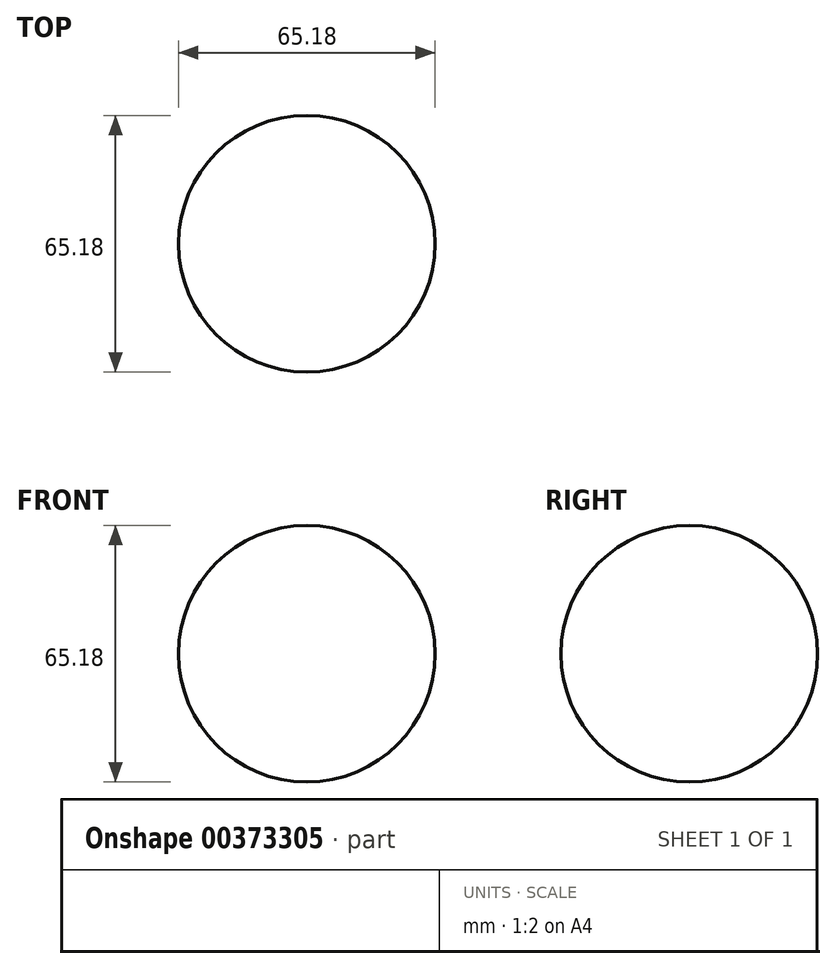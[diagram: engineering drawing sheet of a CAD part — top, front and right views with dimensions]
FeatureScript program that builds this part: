
annotation { "Feature Type Name" : "Feature", "Feature Type Description" : "" }
export const myFeature = defineFeature(function(context is Context, id is Id, definition is map)
    precondition{}
    {
        {
            var Q0;
            Q0=qCreatedBy(makeId("Top.planeOp"),FACE);
            var sketch = newSketch(context, id + "F0", { "sketchPlane" : qUnion([Q0])});
            skArc(sketch, "E0", {"start": v(0, 32.6) * mm, "mid": v(-32.6, 0) * mm, "end": v(0, -32.6) * mm});
            skLineSegment(sketch, "E1", {"start": v(0, 0) * mm, "end": v(0, 55.07) * mm});
            skLineSegment(sketch, "E2", {"start": v(0, 0) * mm, "end": v(0, -54.88) * mm});
            skSolve(sketch);
        }
        {
            var Q0;
            {var subQ0=sQuery(id+"F0.wireOp",EDGE,"E0");Q0=makeQuery(id+"F0.imprint","IMPRINT",FACE,{"disambiguationData":[TD([[makeQuery(id+"F0.imprint","IMPRINT",EDGE,{"derivedFrom":subQ0}),1.0]])]});}
            var Q1;
            Q1=sQuery(id+"F0.wireOp",EDGE,"E1");
            revolve(context, id + "F1", {"entities" : qUnion([Q0]), "axis" : qUnion([Q1]), "revolveType" : RevolveType.FULL});
        }
    });
